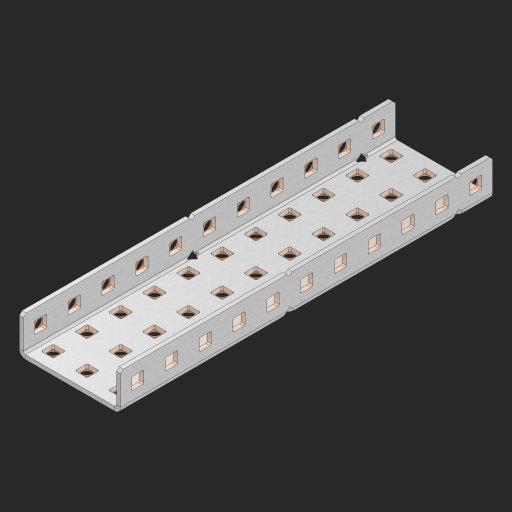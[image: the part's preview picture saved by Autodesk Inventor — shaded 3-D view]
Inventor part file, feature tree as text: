
AUTODESK INVENTOR PART (.ipt)
format: ipt  version: 2023 (Build 270158000, 158)  size: 970,240 bytes
history: native  units: in
note: dims shown in document units (in); Inventor stores cm internally (conversion verified against a paired STEP export)
features: other x60, extrude x54, sheet_metal_op x10, sketch x8, mirror x1, pattern_linear x1, chamfer x1
ambient origin geometry x8: Origin, YZ Plane, XZ Plane, XY Plane, X Axis, Y Axis, Z Axis, Center Point
bodies: Solid1 (feature_tree), Body (feature_tree)
feature tree (135):
  other  "Flange Pattern Plane"
  sheet_metal_op  "Flange Pattern"
  sheet_metal_op  "Body Pattern"
  other  "Arc Length"
  mirror  "Notch Mirror"
  pattern_linear  "Notch Pattern"  Spacing1=0.25in  [1 undecoded]
  chamfer  "End Chamfer"
  extrude  "Half Cut"  Depth=0.0625in
  sketch  "Sketch1"  dims[d0=1.5in]
  other  "Plate1"
  sketch  "Sketch2"  dims[d1=5.5in]
  other  "Plate2"
  sheet_metal_op  "Bend1"
  sheet_metal_op  "Corner1"
  sketch  "Sketch3"  dims[d2=0.0625in]
  other  "Flange Pattern Sketch"
  sketch  "Sketch7"  dims[d3=0.0625in]
  other  "Srf1"
  other  "Srf2"
  sketch  "Sketch8"  dims[d4=0.0312in]
  sketch  "Sketch9"  dims[d5=0.125in]
  other  "Srf91"
  sheet_metal_op  "Body Pattern Sketch"
  other  "Srf92"
  sketch  "Sketch13"  dims[d6=0.0625in]
  sketch  "Sketch14"  dims[d7=0.5in d8=90.0deg d9=0.0312in d10=0.25in d11=0.0625in d12=0.0625in d16=0.182in d17=0.02in d18=0.0625in d19=0.0in d20=0.25in d21=0.25in d46=0.172in d47=1.0in d48=0.0in d49=0.182in d50=0.02in d51=0.25in d52=0.25in d53=0.0625in d54=0.0in d55=0.172in d56=1.0in d57=0.0in d60=4.3307in d62=0.5in d63=1.1811in d65=0.5in d85=0.1473in d86=0.1782in d88=0.04in d89=0.0625in d90=0.0in d91=0.04in d92=0.0491in d95=2.5in d96=0.04in d97=0.25in d98=45.0deg d101=0.0in d102=2.497in d131=1.5in d132=4.3307in d134=0.5in d139=0.5in]
  other  "Srf856"
  other  "Srf1310"
  other  "Srf1311"
  other  "Srf1312"
  other  "Srf1376"
  other  "Srf1377"
  other  "Srf1728"
  other  "Srf1755"
  other  "Srf1878"
  other  "Srf1879"
  other  "Srf1880"
  other  "Srf1881"
  other  "Srf1882"
  other  "Srf1883"
  other  "Srf1884"
  other  "Srf1885"
  other  "Srf1886"
  other  "Srf1887"
  other  "Srf1888"
  other  "Srf1889"
  other  "Srf1890"
  other  "Srf1891"
  other  "Srf1892"
  other  "Srf1893"
  other  "Srf1942"
  other  "Srf1943"
  other  "Srf1944"
  other  "Srf1945"
  other  "Srf1946"
  other  "Srf1947"
  other  "Srf1948"
  other  "Srf1949"
  other  "Srf1950"
  other  "Srf1951"
  other  "Srf1952"
  other  "Srf1953"
  other  "Srf1954"
  other  "Srf1955"
  other  "Srf1956"
  other  "Srf1957"
  other  "Srf1958"
  other  "Srf1959"
  other  "Srf1960"
  other  "Srf1961"
  other  "Srf1962"
  other  "Srf1963"
  other  "Srf1964"
  other  "Srf1965"
  other  "Srf1966"
  other  "Srf1967"
  other  "Srf1968"
  sheet_metal_op  "Flange Stamp"
  sheet_metal_op  "Flange Circle"
  sheet_metal_op  "Body Stamp"
  sheet_metal_op  "Body Circle"
  sheet_metal_op  "Notch"
  extrude  "ExtrusionSrf2"  Depth=0.0625in
  extrude  "ExtrusionSrf92"  Depth=1.5in
  extrude  "ExtrusionSrf856"  Depth=0.02in
  extrude  "ExtrusionSrf1310"  Depth=0.0625in
  extrude  "ExtrusionSrf1311"  TaperAngle=0.0deg  [1 undecoded]
  extrude  "ExtrusionSrf1312"  Depth=0.25in
  extrude  "ExtrusionSrf1376"  Depth=0.25in
  extrude  "ExtrusionSrf1377"  Depth=1.5in
  extrude  "ExtrusionSrf1728"  Depth=1.5in TaperAngle=0.0deg
  extrude  "ExtrusionSrf1755"  Depth=1.5in
  extrude  "ExtrusionSrf1878"  Depth=0.02in
  extrude  "ExtrusionSrf1879"  Depth=0.25in
  extrude  "ExtrusionSrf1880"  Depth=0.25in
  extrude  "ExtrusionSrf1881"  Depth=0.0625in
  extrude  "ExtrusionSrf1882"  TaperAngle=0.0deg  [1 undecoded]
  extrude  "ExtrusionSrf1883"  Depth=1.5in
  extrude  "ExtrusionSrf1884"  Depth=1.5in TaperAngle=0.0deg
  extrude  "ExtrusionSrf1885"  Depth=1.5in
  extrude  "ExtrusionSrf1886"  Depth=1.5in
  extrude  "ExtrusionSrf1887"  Depth=1.5in
  extrude  "ExtrusionSrf1888"  Depth=1.5in
  extrude  "ExtrusionSrf1889"  Depth=1.5in
  extrude  "ExtrusionSrf1890"  Depth=0.0625in
  extrude  "ExtrusionSrf1891"  TaperAngle=0.0deg  [1 undecoded]
  extrude  "ExtrusionSrf1892"  Depth=1.5in
  extrude  "ExtrusionSrf1893"  Depth=1.5in
  extrude  "ExtrusionSrf1942"  Depth=1.5in
  extrude  "ExtrusionSrf1943"  Depth=0.25in TaperAngle=45.0deg
  extrude  "ExtrusionSrf1944"  TaperAngle=0.0deg  [1 undecoded]
  extrude  "ExtrusionSrf1945"  Depth=1.5in
  extrude  "ExtrusionSrf1946"  Depth=1.5in
  extrude  "ExtrusionSrf1947"  Depth=1.5in
  extrude  "ExtrusionSrf1948"  Depth=1.5in
  extrude  "ExtrusionSrf1949"  Depth=1.5in
  extrude  "ExtrusionSrf1950"  [1 undecoded]
  extrude  "ExtrusionSrf1951"  [1 undecoded]
  extrude  "ExtrusionSrf1952"  [1 undecoded]
  extrude  "ExtrusionSrf1953"  [1 undecoded]
  extrude  "ExtrusionSrf1954"  [1 undecoded]
  extrude  "ExtrusionSrf1955"  [1 undecoded]
  extrude  "ExtrusionSrf1956"  [1 undecoded]
  extrude  "ExtrusionSrf1957"  [1 undecoded]
  extrude  "ExtrusionSrf1958"  [1 undecoded]
  extrude  "ExtrusionSrf1959"  [1 undecoded]
  extrude  "ExtrusionSrf1960"  [1 undecoded]
  extrude  "ExtrusionSrf1961"  [1 undecoded]
  extrude  "ExtrusionSrf1962"  [1 undecoded]
  extrude  "ExtrusionSrf1963"  [1 undecoded]
  extrude  "ExtrusionSrf1964"  [1 undecoded]
  extrude  "ExtrusionSrf1965"  [1 undecoded]
  extrude  "ExtrusionSrf1966"  [1 undecoded]
  extrude  "ExtrusionSrf1967"  [1 undecoded]
  extrude  "ExtrusionSrf1968"  [1 undecoded]
note: 24 required parameter values undecoded (feature->parameter linkage not recoverable at this tier; creation-order binding heuristic only, values carry confidence <= 0.55)
